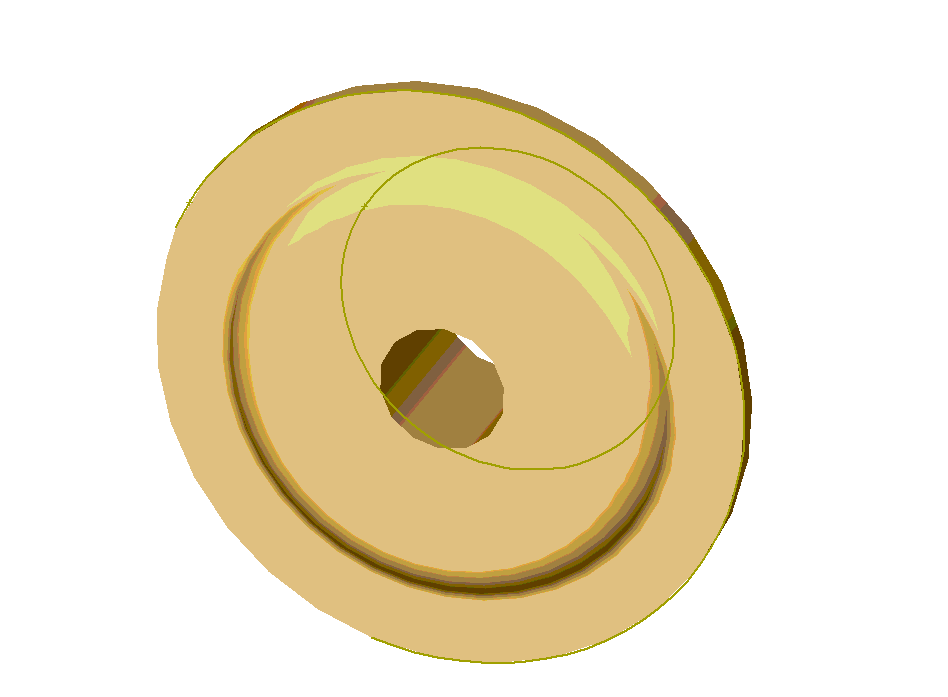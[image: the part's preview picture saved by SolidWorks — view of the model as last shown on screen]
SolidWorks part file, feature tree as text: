
SOLIDWORKS PART (.sldprt)
format: sldprt  version: not decoded by parser v0  size: 161,280 bytes
history: native  units: mm
features: sketch x8, extrude x4, plane x3, fillet x2, cut_extrude x2, material x1, helix x1, sweep x1 (+8 scaffold rows collapsed)
feature tree (30):
  scaffold x8  (default folders/planes/origin — collapsed)
  material  "Matériau <non spécifié>"
  plane  "Face"
  plane  "Dessus"
  plane  "Droite"
  sketch  "Esquisse1"  dims[D1=2.0mm]
  helix  "Hélice1"  Pitch=6mm
  sketch  "Esquisse8"  dims[D1=~0.15227mm]
  sweep  "Base-Balayage"
  sketch  "Esquisse9"  dims[D1=~4.745564mm]
  extrude  "Boss.-Extru.1"  Depth=0.3mm
  sketch  "Esquisse10"  dims[D1=~2.288095mm]
  extrude  "Boss.-Extru.2"  Depth=0.5mm
  fillet  "Congé1"  Radius=0.5mm
  fillet  "Congé2"  Radius=0.2mm
  sketch  "Esquisse11"  dims[D1=~1.535483mm]
  extrude  "Boss.-Extru.3"  Depth=2mm
  sketch  "Esquisse12"  dims[D1=~1.072338mm]
  cut_extrude  "Enlèv. mat.-Extru.1"  [1 undecoded]
  sketch  "Esquisse13"  dims[D1=~1.881813mm]
  extrude  "Boss.-Extru.4"  Depth=0.2mm
  sketch  "Esquisse14"  dims[D1=~4.027633mm]
  cut_extrude  "Enlèv. mat.-Extru.2"  Depth=30mm
decode coverage: 16 of 18 modeling features carry decoded parameters
note: ~ marks probable driven/reference dimensions
note: 1 parameter value undecoded
note: suppression state not decoded; provenance and decode notes live in map.json
